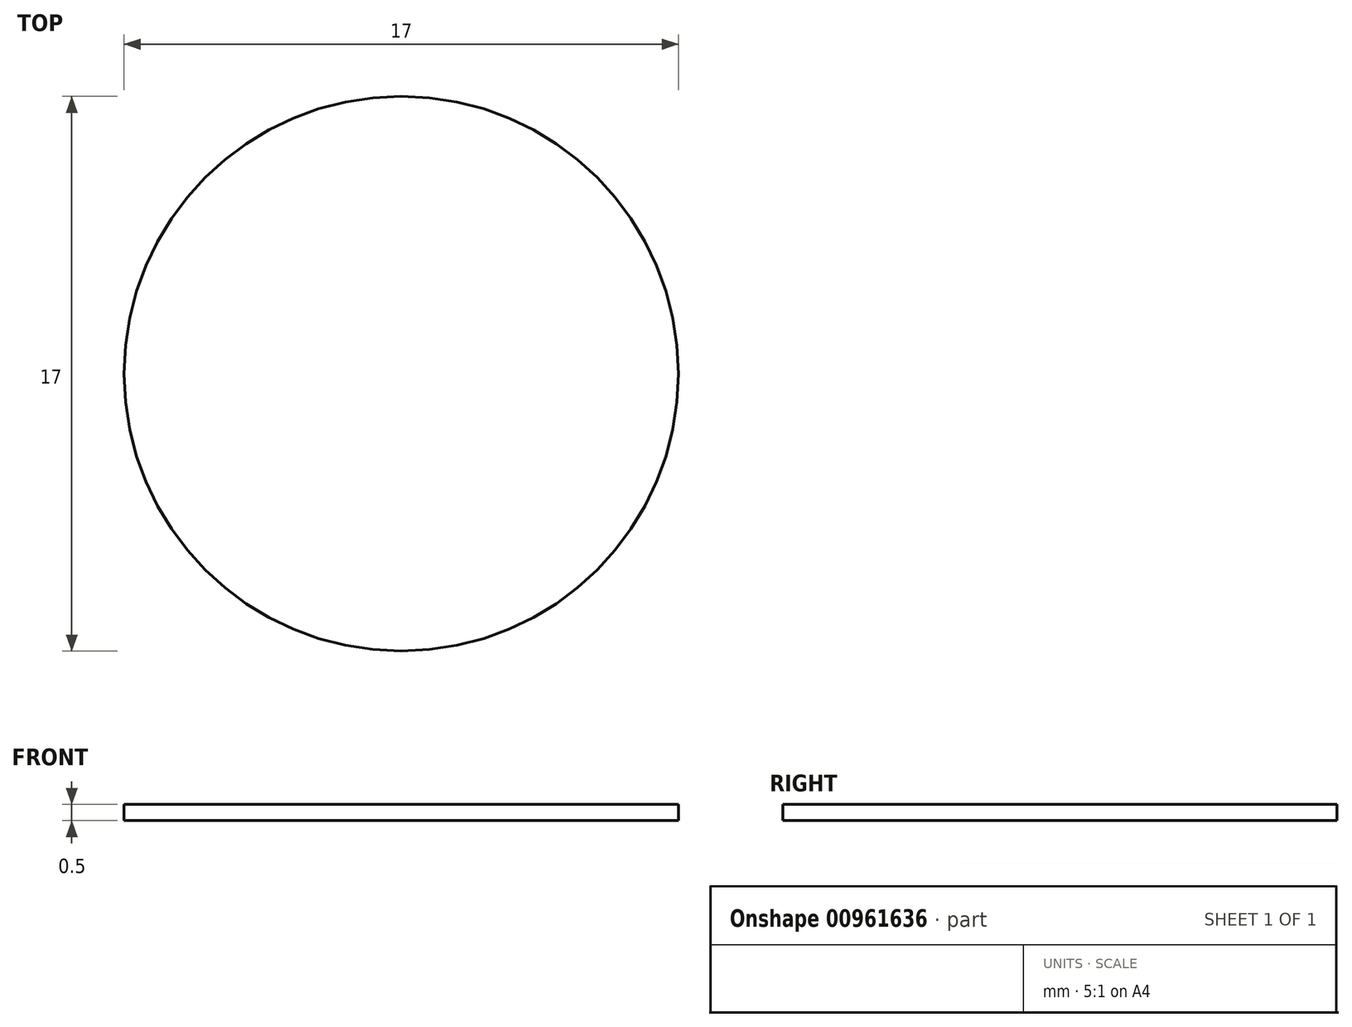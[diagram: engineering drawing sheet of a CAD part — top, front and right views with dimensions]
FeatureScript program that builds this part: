
annotation { "Feature Type Name" : "Feature", "Feature Type Description" : "" }
export const myFeature = defineFeature(function(context is Context, id is Id, definition is map)
    precondition{}
    {
        {
            var Q0;
            Q0=qCreatedBy(makeId("Top.planeOp"),FACE);
            var sketch = newSketch(context, id + "F0", { "sketchPlane" : qUnion([Q0])});
            skCircle(sketch, "E0", {"center": v(0, 0) * mm, "radius": 8.5 * mm});
            skSolve(sketch);
        }
        {
            var Q0;
            Q0=qSketchRegion(id+"F0",true);
            extrude(context, id + "F1", {"entities" : qUnion([Q0]), "depth" : 0.5 * mm, "offsetDistance" : 25 * mm});
        }
    });
